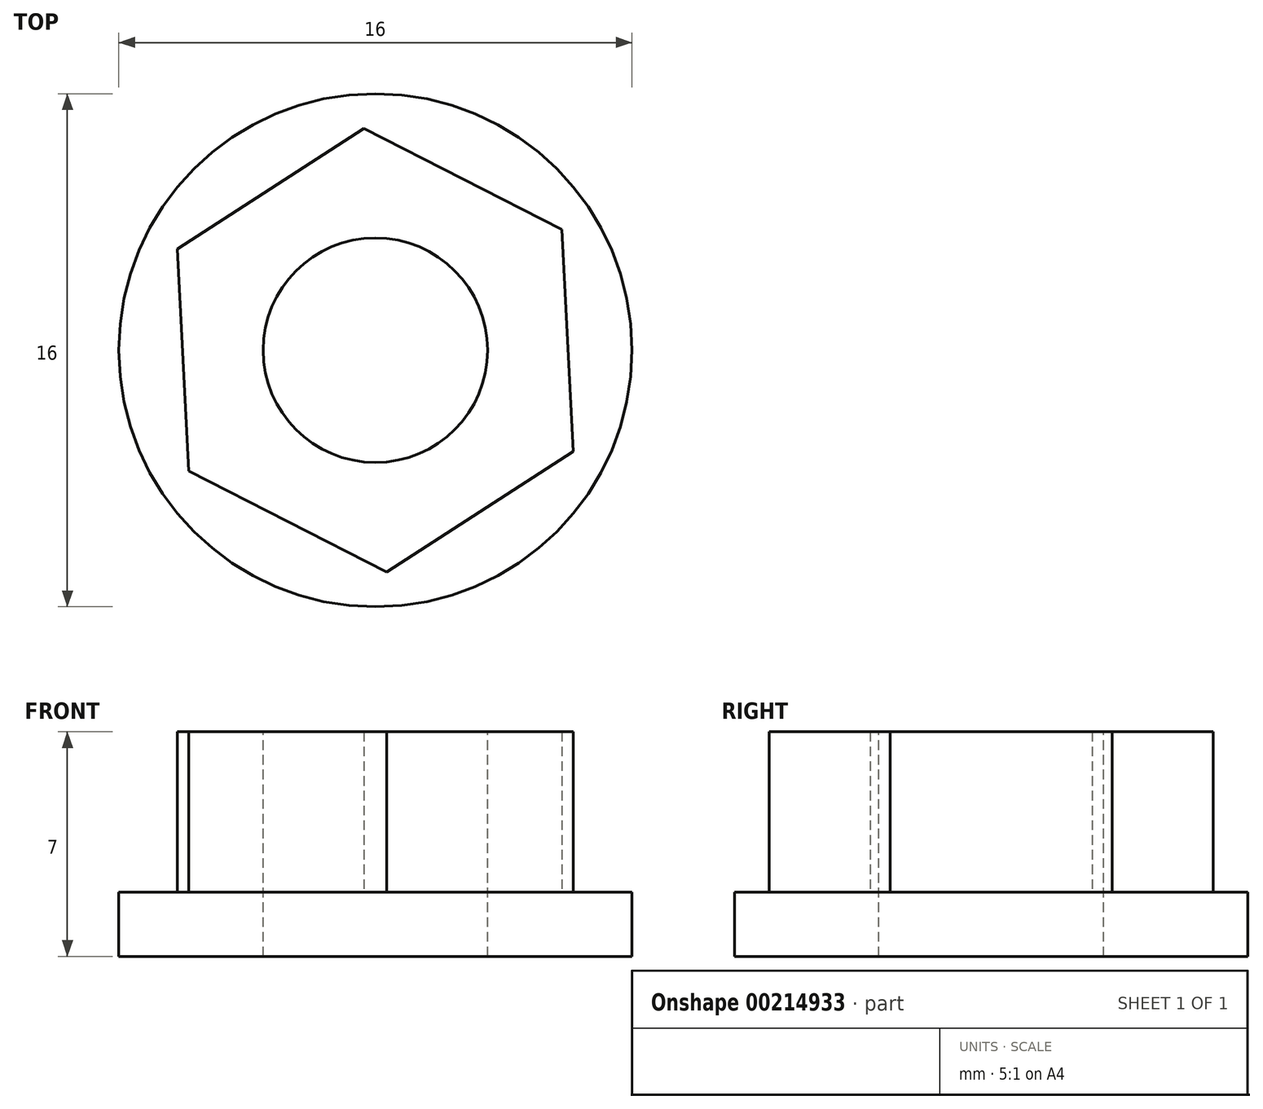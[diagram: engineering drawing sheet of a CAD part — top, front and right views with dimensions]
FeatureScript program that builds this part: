
annotation { "Feature Type Name" : "Feature", "Feature Type Description" : "" }
export const myFeature = defineFeature(function(context is Context, id is Id, definition is map)
    precondition{}
    {
        {
            var Q0;
            Q0=qCreatedBy(makeId("Top.planeOp"),FACE);
            var sketch = newSketch(context, id + "F0", { "sketchPlane" : qUnion([Q0])});
            skCircle(sketch, "E0", {"center": v(0, 0) * mm, "radius": 8 * mm});
            skSolve(sketch);
        }
        {
            var Q0;
            Q0 = qSketchRegion(id + "F0", true);
            var Q1;
            Q1=makeQuery(id+"F0.imprint","IMPRINT",FACE,{"disambiguationData":[TD([[makeQuery(id+"F0.imprint","IMPRINT",EDGE,{"derivedFrom":sQuery(id+"F0.wireOp",EDGE,"E0")}),1.0]])]});
            extrude(context, id + "F1", {"entities" : qUnion([Q0, Q1]), "depth" : 2 * mm, "offsetDistance" : 25 * mm});
        }
        {
            var Q0;
            Q0=makeQuery(id+"F1.opExtrude","CAP_FACE",FACE,{"disambiguationData":[OSD([sQuery(id+"F0.wireOp",EDGE,"E0")])],"isStart":false});
            var sketch = newSketch(context, id + "F2", { "sketchPlane" : qUnion([Q0])});
            skCircle(sketch, "E1.cCircle", {"center": v(0, 0) * mm, "radius": 6 * mm, "construction": true});
            skLineSegment(sketch, "E1.0", {"start": v(-0.36, 6.92) * mm, "end": v(5.81, 3.77) * mm});
            skLineSegment(sketch, "E1.1", {"start": v(5.81, 3.77) * mm, "end": v(6.17, -3.15) * mm});
            skLineSegment(sketch, "E1.2", {"start": v(6.17, -3.15) * mm, "end": v(0.36, -6.92) * mm});
            skLineSegment(sketch, "E1.3", {"start": v(0.36, -6.92) * mm, "end": v(-5.81, -3.77) * mm});
            skLineSegment(sketch, "E1.4", {"start": v(-5.81, -3.77) * mm, "end": v(-6.17, 3.15) * mm});
            skLineSegment(sketch, "E1.5", {"start": v(-6.17, 3.15) * mm, "end": v(-0.36, 6.92) * mm});
            skPoint(sketch, "E1.0.midPoint", {"position": v(2.73, 5.34) * mm});
            skSolve(sketch);
        }
        {
            var Q0;
            Q0=makeQuery(id+"F2.imprint","IMPRINT",FACE,{"disambiguationData":[TD([[makeQuery(id+"F2.imprint","IMPRINT",EDGE,{"derivedFrom":sQuery(id+"F2.wireOp",EDGE,"E1.0")}),-1.0]])]});
            extrude(context, id + "F3", {"entities" : qUnion([Q0]), "operationType" : NewBodyOperationType.ADD, "depth" : 5 * mm, "offsetDistance" : 25 * mm});
        }
        {
            var Q0;
            Q0=makeQuery(id+"F3.opExtrude","CAP_FACE",FACE,{"disambiguationData":[OSD([sQuery(id+"F2.wireOp",EDGE,"E1.0"),sQuery(id+"F2.wireOp",EDGE,"E1.1"),sQuery(id+"F2.wireOp",EDGE,"E1.2"),sQuery(id+"F2.wireOp",EDGE,"E1.3"),sQuery(id+"F2.wireOp",EDGE,"E1.4"),sQuery(id+"F2.wireOp",EDGE,"E1.5")])],"isStart":false});
            var sketch = newSketch(context, id + "F4", { "sketchPlane" : qUnion([Q0])});
            skCircle(sketch, "E2", {"center": v(0, 0) * mm, "radius": 3.5 * mm});
            skSolve(sketch);
        }
        {
            var Q0;
            Q0=makeQuery(id+"F4.imprint","IMPRINT",FACE,{"disambiguationData":[TD([[makeQuery(id+"F4.imprint","IMPRINT",EDGE,{"derivedFrom":sQuery(id+"F4.wireOp",EDGE,"E2")}),1.0]])]});
            extrude(context, id + "F5", {"entities" : qUnion([Q0]), "operationType" : NewBodyOperationType.REMOVE, "oppositeDirection" : true, "depth" : 25 * mm, "offsetDistance" : 25 * mm});
        }
    });
